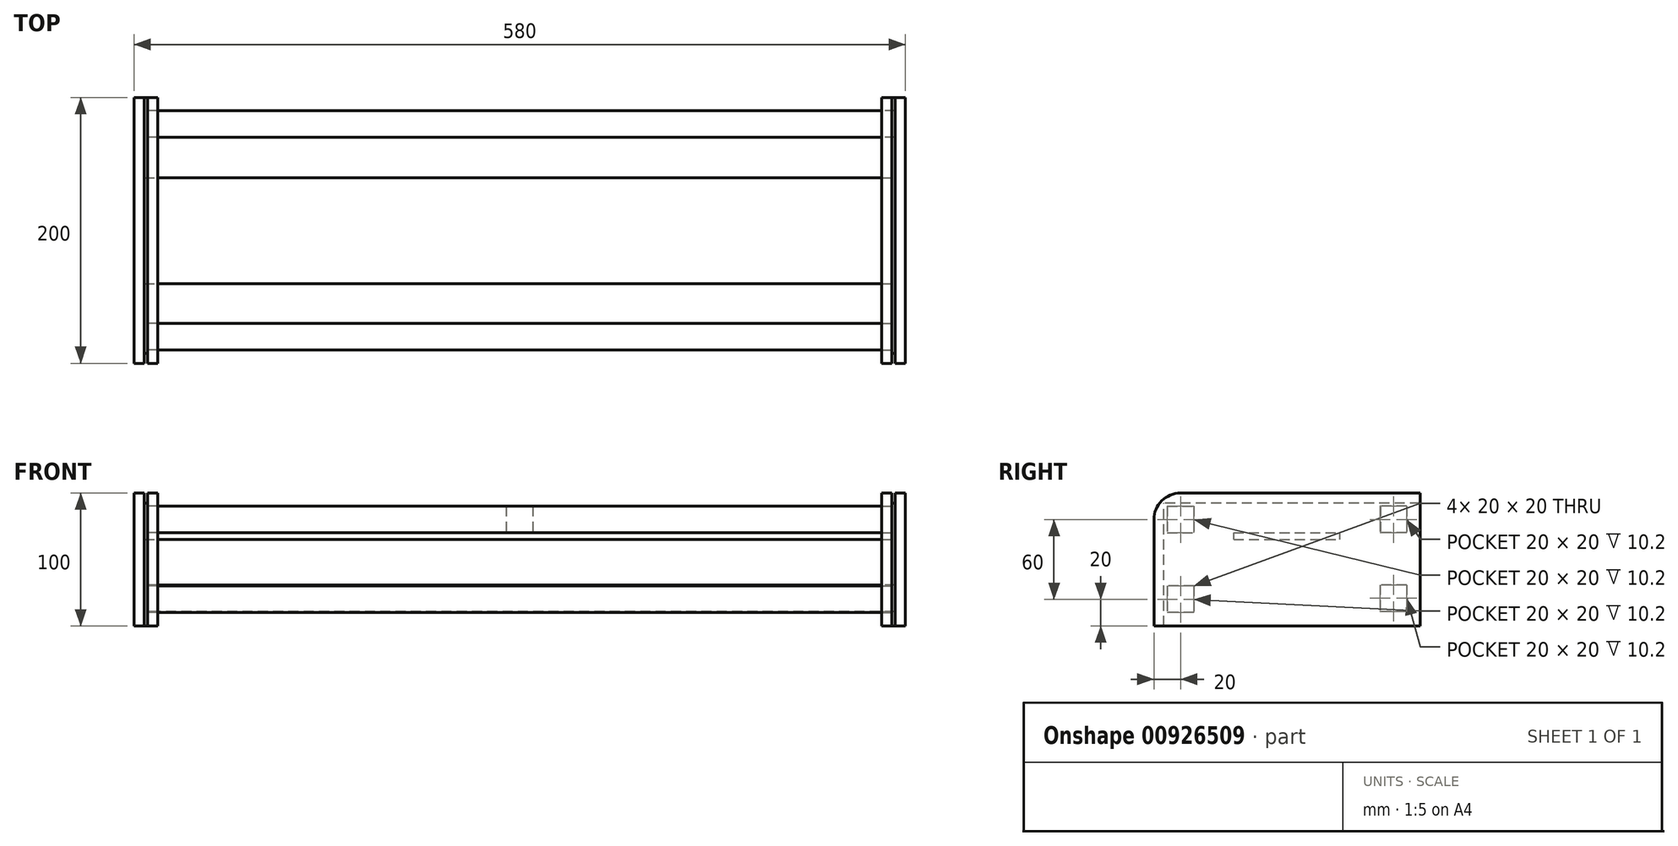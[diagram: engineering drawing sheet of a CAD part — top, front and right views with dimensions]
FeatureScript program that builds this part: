
annotation { "Feature Type Name" : "Feature", "Feature Type Description" : "" }
export const myFeature = defineFeature(function(context is Context, id is Id, definition is map)
    precondition{}
    {
        {
            var Q0;
            Q0=qCreatedBy(makeId("Right.planeOp"),FACE);
            var sketch = newSketch(context, id + "F0", { "sketchPlane" : qUnion([Q0])});
            skLineSegment(sketch, "E0.bottom", {"start": v(100, -50) * mm, "end": v(-100, -50) * mm});
            skLineSegment(sketch, "E0.top", {"start": v(100, 50) * mm, "end": v(-100, 50) * mm});
            skLineSegment(sketch, "E0.left", {"start": v(100, -50) * mm, "end": v(100, 50) * mm});
            skLineSegment(sketch, "E0.right", {"start": v(-100, -50) * mm, "end": v(-100, 50) * mm});
            skPoint(sketch, "E0.middle", {"position": v(0, 0) * mm});
            skLineSegment(sketch, "E1.bottom", {"start": v(80, -30) * mm, "end": v(-80, -30) * mm});
            skLineSegment(sketch, "E1.top", {"start": v(80, 30) * mm, "end": v(-80, 30) * mm});
            skLineSegment(sketch, "E1.left", {"start": v(80, -30) * mm, "end": v(80, 30) * mm});
            skLineSegment(sketch, "E1.right", {"start": v(-80, -30) * mm, "end": v(-80, 30) * mm});
            skLineSegment(sketch, "E2.right", {"start": v(-90, -36.84) * mm, "end": v(-80, -33.46) * mm});
            skPoint(sketch, "E2.middle", {"position": v(0, -31.3) * mm});
            skLineSegment(sketch, "E3.right", {"start": v(-89.73, 15.73) * mm, "end": v(-80, 14.19) * mm});
            skPoint(sketch, "E3.middle", {"position": v(0, 23.38) * mm});
            skLineSegment(sketch, "E4.bottom", {"start": v(16.66, -50) * mm, "end": v(-14.9, -50) * mm});
            skLineSegment(sketch, "E4.top", {"start": v(14.9, 50) * mm, "end": v(-16.66, 50) * mm});
            skLineSegment(sketch, "E5.left", {"start": v(100, -5.01) * mm, "end": v(100, 5.01) * mm});
            skLineSegment(sketch, "E5.right", {"start": v(-100, -5.01) * mm, "end": v(-100, 5.01) * mm});
            skLineSegment(sketch, "E6.bottom", {"start": v(70, 20) * mm, "end": v(90, 20) * mm});
            skLineSegment(sketch, "E6.top", {"start": v(70, 40) * mm, "end": v(90, 40) * mm});
            skLineSegment(sketch, "E6.left", {"start": v(70, 20) * mm, "end": v(70, 40) * mm});
            skLineSegment(sketch, "E6.right", {"start": v(90, 20) * mm, "end": v(90, 40) * mm});
            skPoint(sketch, "E6.middle", {"position": v(80, 30) * mm});
            skLineSegment(sketch, "E7.bottom", {"start": v(-70, 20) * mm, "end": v(-90, 20) * mm});
            skLineSegment(sketch, "E7.top", {"start": v(-70, 40) * mm, "end": v(-90, 40) * mm});
            skLineSegment(sketch, "E7.left", {"start": v(-70, 20) * mm, "end": v(-70, 40) * mm});
            skLineSegment(sketch, "E7.right", {"start": v(-90, 20) * mm, "end": v(-90, 40) * mm});
            skPoint(sketch, "E7.middle", {"position": v(-80, 30) * mm});
            skLineSegment(sketch, "E8.bottom", {"start": v(-90, -40) * mm, "end": v(-70, -40) * mm});
            skLineSegment(sketch, "E8.top", {"start": v(-90, -20) * mm, "end": v(-70, -20) * mm});
            skLineSegment(sketch, "E8.left", {"start": v(-90, -40) * mm, "end": v(-90, -20) * mm});
            skLineSegment(sketch, "E8.right", {"start": v(-70, -40) * mm, "end": v(-70, -20) * mm});
            skPoint(sketch, "E8.middle", {"position": v(-80, -30) * mm});
            skLineSegment(sketch, "E9.bottom", {"start": v(70, -39.16) * mm, "end": v(90, -39.16) * mm});
            skLineSegment(sketch, "E9.top", {"start": v(70, -19.16) * mm, "end": v(90, -19.16) * mm});
            skLineSegment(sketch, "E9.left", {"start": v(70, -39.16) * mm, "end": v(70, -19.16) * mm});
            skLineSegment(sketch, "E9.right", {"start": v(90, -39.16) * mm, "end": v(90, -19.16) * mm});
            skPoint(sketch, "E9.middle", {"position": v(80, -29.16) * mm});
            skSolve(sketch);
        }
        {
            var Q0;
            {var subQ10=sQuery(id+"F0.wireOp",EDGE,"E0.left");Q0=makeQuery(id+"F0.imprint","IMPRINT",FACE,{"disambiguationData":[TD([[makeQuery(id+"F0.imprint","IMPRINT",EDGE,{"derivedFrom":subQ10}),1.0]])]});}
            var Q1;
            {var subQ14=sQuery(id+"F0.wireOp",EDGE,"E0.right");Q1=makeQuery(id+"F0.imprint","IMPRINT",FACE,{"disambiguationData":[TD([[makeQuery(id+"F0.imprint","IMPRINT",EDGE,{"derivedFrom":subQ14}),-1.0]])]});}
            var Q2;
            {var subQ1=sQuery(id+"F0.wireOp",EDGE,"E4.top");Q2=makeQuery(id+"F0.imprint","IMPRINT",FACE,{"disambiguationData":[TD([[makeQuery(id+"F0.imprint","IMPRINT",EDGE,{"derivedFrom":subQ1}),1.0]])]});}
            var Q3;
            {var subQ0=sQuery(id+"F0.wireOp",EDGE,"E3.top");var subQ1=sQuery(id+"F0.wireOp",EDGE,"ilXIjhRa-h4DM-NYfa-dKmE-4tYrYaVo3qCb");var subQ2=makeQuery(id+"F0.imprint","INTERSECT",VERTEX,{"disambiguationData":[OD(1.0)],"derivedFrom":[subQ1,subQ0]});Q3=makeQuery(id+"F0.imprint","IMPRINT",FACE,{"disambiguationData":[TD([[makeQuery(id+"F0.imprint","IMPRINT",EDGE,{"disambiguationData":[TD([[subQ2,-1.0]])],"derivedFrom":subQ1}),1.0]])]});}
            var Q4;
            {var subQ0=sQuery(id+"F0.wireOp",EDGE,"E3.bottom");var subQ1=sQuery(id+"F0.wireOp",EDGE,"ilXIjhRa-h4DM-NYfa-dKmE-4tYrYaVo3qCb");var subQ2=makeQuery(id+"F0.imprint","INTERSECT",VERTEX,{"disambiguationData":[OD(1.0)],"derivedFrom":[subQ1,subQ0]});Q4=makeQuery(id+"F0.imprint","IMPRINT",FACE,{"disambiguationData":[TD([[makeQuery(id+"F0.imprint","IMPRINT",EDGE,{"disambiguationData":[TD([[subQ2,-1.0]])],"derivedFrom":subQ1}),1.0]])]});}
            var Q5;
            {var subQ0=sQuery(id+"F0.wireOp",EDGE,"E2.top");var subQ1=sQuery(id+"F0.wireOp",EDGE,"ilXIjhRa-h4DM-NYfa-dKmE-4tYrYaVo3qCb");var subQ2=makeQuery(id+"F0.imprint","INTERSECT",VERTEX,{"disambiguationData":[OD(0.0)],"derivedFrom":[subQ1,subQ0]});Q5=makeQuery(id+"F0.imprint","IMPRINT",FACE,{"disambiguationData":[TD([[makeQuery(id+"F0.imprint","IMPRINT",EDGE,{"disambiguationData":[TD([[subQ2,-1.0]])],"derivedFrom":subQ1}),1.0]])]});}
            var Q6;
            {var subQ0=sQuery(id+"F0.wireOp",EDGE,"E4.bottom");Q6=makeQuery(id+"F0.imprint","IMPRINT",FACE,{"disambiguationData":[TD([[makeQuery(id+"F0.imprint","IMPRINT",EDGE,{"derivedFrom":subQ0}),-1.0]])]});}
            var Q7;
            {var subQ0=sQuery(id+"F0.wireOp",EDGE,"E2.bottom");var subQ1=sQuery(id+"F0.wireOp",EDGE,"ilXIjhRa-h4DM-NYfa-dKmE-4tYrYaVo3qCb");var subQ2=makeQuery(id+"F0.imprint","INTERSECT",VERTEX,{"disambiguationData":[OD(1.0)],"derivedFrom":[subQ1,subQ0]});Q7=makeQuery(id+"F0.imprint","IMPRINT",FACE,{"disambiguationData":[TD([[makeQuery(id+"F0.imprint","IMPRINT",EDGE,{"disambiguationData":[TD([[subQ2,-1.0]])],"derivedFrom":subQ1}),1.0]])]});}
            var Q8;
            {var subQ0=sQuery(id+"F0.wireOp",EDGE,"E3.top");var subQ1=sQuery(id+"F0.wireOp",EDGE,"ilXIjhRa-h4DM-NYfa-dKmE-4tYrYaVo3qCb");var subQ2=makeQuery(id+"F0.imprint","INTERSECT",VERTEX,{"disambiguationData":[OD(0.0)],"derivedFrom":[subQ1,subQ0]});Q8=makeQuery(id+"F0.imprint","IMPRINT",FACE,{"disambiguationData":[TD([[makeQuery(id+"F0.imprint","IMPRINT",EDGE,{"disambiguationData":[TD([[subQ2,1.0]])],"derivedFrom":subQ1}),1.0]])]});}
            var Q9;
            {var subQ0=sQuery(id+"F0.wireOp",EDGE,"E3.bottom");var subQ1=sQuery(id+"F0.wireOp",EDGE,"ilXIjhRa-h4DM-NYfa-dKmE-4tYrYaVo3qCb");var subQ2=makeQuery(id+"F0.imprint","INTERSECT",VERTEX,{"disambiguationData":[OD(0.0)],"derivedFrom":[subQ1,subQ0]});Q9=makeQuery(id+"F0.imprint","IMPRINT",FACE,{"disambiguationData":[TD([[makeQuery(id+"F0.imprint","IMPRINT",EDGE,{"disambiguationData":[TD([[subQ2,1.0]])],"derivedFrom":subQ1}),1.0]])]});}
            var Q10;
            {var subQ0=sQuery(id+"F0.wireOp",EDGE,"E4.left");var subQ1=sQuery(id+"F0.wireOp",EDGE,"E3.bottom");var subQ2=makeQuery(id+"F0.imprint","INTERSECT",VERTEX,{"derivedFrom":[subQ1,subQ0]});Q10=makeQuery(id+"F0.imprint","IMPRINT",FACE,{"disambiguationData":[TD([[makeQuery(id+"F0.imprint","IMPRINT",EDGE,{"disambiguationData":[TD([[subQ2,-1.0]])],"derivedFrom":subQ1}),-1.0]])]});}
            var Q11;
            {var subQ1=sQuery(id+"F0.wireOp",EDGE,"qJEwsRZI-Cwcr-TwOn-KfsY-0AIqheChsfac");var subQ7=makeQuery(id+"F0.imprint","INTERSECT",VERTEX,{"derivedFrom":[sQuery(id+"F0.wireOp",EDGE,"E1.top"),subQ1]});Q11=makeQuery(id+"F0.imprint","IMPRINT",FACE,{"disambiguationData":[TD([[makeQuery(id+"F0.imprint","IMPRINT",EDGE,{"disambiguationData":[TD([[subQ7,1.0]])],"derivedFrom":subQ1}),1.0]])]});}
            var Q12;
            {var subQ5=sQuery(id+"F0.wireOp",EDGE,"qJEwsRZI-Cwcr-TwOn-KfsY-0AIqheChsfac");var subQ7=makeQuery(id+"F0.imprint","INTERSECT",VERTEX,{"derivedFrom":[sQuery(id+"F0.wireOp",EDGE,"E1.bottom"),subQ5]});Q12=makeQuery(id+"F0.imprint","IMPRINT",FACE,{"disambiguationData":[TD([[makeQuery(id+"F0.imprint","IMPRINT",EDGE,{"disambiguationData":[TD([[subQ7,1.0]])],"derivedFrom":subQ5}),1.0]])]});}
            var Q13;
            {var subQ0=sQuery(id+"F0.wireOp",EDGE,"E4.left");var subQ1=sQuery(id+"F0.wireOp",EDGE,"E2.top");var subQ2=makeQuery(id+"F0.imprint","INTERSECT",VERTEX,{"derivedFrom":[subQ1,subQ0]});Q13=makeQuery(id+"F0.imprint","IMPRINT",FACE,{"disambiguationData":[TD([[makeQuery(id+"F0.imprint","IMPRINT",EDGE,{"disambiguationData":[TD([[subQ2,-1.0]])],"derivedFrom":subQ1}),-1.0]])]});}
            var Q14;
            {var subQ0=sQuery(id+"F0.wireOp",EDGE,"E2.top");var subQ1=sQuery(id+"F0.wireOp",EDGE,"qJEwsRZI-Cwcr-TwOn-KfsY-0AIqheChsfac");var subQ2=makeQuery(id+"F0.imprint","INTERSECT",VERTEX,{"disambiguationData":[OD(0.0)],"derivedFrom":[subQ1,subQ0]});Q14=makeQuery(id+"F0.imprint","IMPRINT",FACE,{"disambiguationData":[TD([[makeQuery(id+"F0.imprint","IMPRINT",EDGE,{"disambiguationData":[TD([[subQ2,-1.0]])],"derivedFrom":subQ1}),1.0]])]});}
            var Q15;
            {var subQ0=sQuery(id+"F0.wireOp",EDGE,"E2.bottom");var subQ1=sQuery(id+"F0.wireOp",EDGE,"qJEwsRZI-Cwcr-TwOn-KfsY-0AIqheChsfac");var subQ2=makeQuery(id+"F0.imprint","INTERSECT",VERTEX,{"disambiguationData":[OD(1.0)],"derivedFrom":[subQ1,subQ0]});Q15=makeQuery(id+"F0.imprint","IMPRINT",FACE,{"disambiguationData":[TD([[makeQuery(id+"F0.imprint","IMPRINT",EDGE,{"disambiguationData":[TD([[subQ2,-1.0]])],"derivedFrom":subQ1}),1.0]])]});}
            var Q16;
            {var subQ3=sQuery(id+"F0.wireOp",EDGE,"E3.bottom");var subQ5=sQuery(id+"F0.wireOp",EDGE,"ilXIjhRa-h4DM-NYfa-dKmE-4tYrYaVo3qCb");var subQ7=makeQuery(id+"F0.imprint","INTERSECT",VERTEX,{"disambiguationData":[OD(1.0)],"derivedFrom":[subQ5,subQ3]});Q16=makeQuery(id+"F0.imprint","IMPRINT",FACE,{"disambiguationData":[TD([[makeQuery(id+"F0.imprint","IMPRINT",EDGE,{"disambiguationData":[TD([[subQ7,-1.0]])],"derivedFrom":subQ5}),-1.0]])]});}
            var Q17;
            {var subQ3=sQuery(id+"F0.wireOp",EDGE,"E3.bottom");var subQ5=sQuery(id+"F0.wireOp",EDGE,"ilXIjhRa-h4DM-NYfa-dKmE-4tYrYaVo3qCb");var subQ6=makeQuery(id+"F0.imprint","INTERSECT",VERTEX,{"disambiguationData":[OD(0.0)],"derivedFrom":[subQ5,subQ3]});Q17=makeQuery(id+"F0.imprint","IMPRINT",FACE,{"disambiguationData":[TD([[makeQuery(id+"F0.imprint","IMPRINT",EDGE,{"disambiguationData":[TD([[subQ6,1.0]])],"derivedFrom":subQ5}),-1.0]])]});}
            var Q18;
            {var subQ0=sQuery(id+"F0.wireOp",EDGE,"E3.bottom");var subQ1=sQuery(id+"F0.wireOp",EDGE,"qJEwsRZI-Cwcr-TwOn-KfsY-0AIqheChsfac");var subQ2=makeQuery(id+"F0.imprint","INTERSECT",VERTEX,{"disambiguationData":[OD(1.0)],"derivedFrom":[subQ1,subQ0]});Q18=makeQuery(id+"F0.imprint","IMPRINT",FACE,{"disambiguationData":[TD([[makeQuery(id+"F0.imprint","IMPRINT",EDGE,{"disambiguationData":[TD([[subQ2,-1.0]])],"derivedFrom":subQ1}),1.0]])]});}
            var Q19;
            {var subQ0=sQuery(id+"F0.wireOp",EDGE,"E3.bottom");var subQ1=sQuery(id+"F0.wireOp",EDGE,"qJEwsRZI-Cwcr-TwOn-KfsY-0AIqheChsfac");var subQ2=makeQuery(id+"F0.imprint","INTERSECT",VERTEX,{"disambiguationData":[OD(0.0)],"derivedFrom":[subQ1,subQ0]});Q19=makeQuery(id+"F0.imprint","IMPRINT",FACE,{"disambiguationData":[TD([[makeQuery(id+"F0.imprint","IMPRINT",EDGE,{"disambiguationData":[TD([[subQ2,1.0]])],"derivedFrom":subQ1}),1.0]])]});}
            var Q20;
            {var subQ0=sQuery(id+"F0.wireOp",EDGE,"E3.top");var subQ1=sQuery(id+"F0.wireOp",EDGE,"qJEwsRZI-Cwcr-TwOn-KfsY-0AIqheChsfac");var subQ2=makeQuery(id+"F0.imprint","INTERSECT",VERTEX,{"disambiguationData":[OD(0.0)],"derivedFrom":[subQ1,subQ0]});Q20=makeQuery(id+"F0.imprint","IMPRINT",FACE,{"disambiguationData":[TD([[makeQuery(id+"F0.imprint","IMPRINT",EDGE,{"disambiguationData":[TD([[subQ2,-1.0]])],"derivedFrom":subQ1}),1.0]])]});}
            var Q21;
            {var subQ0=sQuery(id+"F0.wireOp",EDGE,"E4.right");var subQ1=sQuery(id+"F0.wireOp",EDGE,"qJEwsRZI-Cwcr-TwOn-KfsY-0AIqheChsfac");var subQ2=makeQuery(id+"F0.imprint","INTERSECT",VERTEX,{"disambiguationData":[OD(0.0)],"derivedFrom":[subQ1,subQ0]});Q21=makeQuery(id+"F0.imprint","IMPRINT",FACE,{"disambiguationData":[TD([[makeQuery(id+"F0.imprint","IMPRINT",EDGE,{"disambiguationData":[TD([[subQ2,-1.0]])],"derivedFrom":subQ1}),1.0]])]});}
            var Q22;
            {var subQ0=sQuery(id+"F0.wireOp",EDGE,"E4.left");var subQ1=sQuery(id+"F0.wireOp",EDGE,"qJEwsRZI-Cwcr-TwOn-KfsY-0AIqheChsfac");var subQ2=makeQuery(id+"F0.imprint","INTERSECT",VERTEX,{"disambiguationData":[OD(1.0)],"derivedFrom":[subQ1,subQ0]});Q22=makeQuery(id+"F0.imprint","IMPRINT",FACE,{"disambiguationData":[TD([[makeQuery(id+"F0.imprint","IMPRINT",EDGE,{"disambiguationData":[TD([[subQ2,-1.0]])],"derivedFrom":subQ1}),1.0]])]});}
            var Q23;
            {var subQ0=sQuery(id+"F0.wireOp",EDGE,"E2.bottom");var subQ1=sQuery(id+"F0.wireOp",EDGE,"qJEwsRZI-Cwcr-TwOn-KfsY-0AIqheChsfac");var subQ2=makeQuery(id+"F0.imprint","INTERSECT",VERTEX,{"disambiguationData":[OD(0.0)],"derivedFrom":[subQ1,subQ0]});Q23=makeQuery(id+"F0.imprint","IMPRINT",FACE,{"disambiguationData":[TD([[makeQuery(id+"F0.imprint","IMPRINT",EDGE,{"disambiguationData":[TD([[subQ2,-1.0]])],"derivedFrom":subQ1}),1.0]])]});}
            var Q24;
            {var subQ0=sQuery(id+"F0.wireOp",EDGE,"c1IAvuGv-3G2W-eEcT-URjF-tdlOrtGlBp0P");var subQ1=sQuery(id+"F0.wireOp",EDGE,"E0.top");var subQ2=makeQuery(id+"F0.imprint","INTERSECT",VERTEX,{"disambiguationData":[OD(1.0)],"derivedFrom":[subQ1,subQ0]});Q24=makeQuery(id+"F0.imprint","IMPRINT",FACE,{"disambiguationData":[TD([[makeQuery(id+"F0.imprint","IMPRINT",EDGE,{"disambiguationData":[TD([[subQ2,1.0]])],"derivedFrom":subQ1}),1.0]])]});}
            var Q25;
            {var subQ0=sQuery(id+"F0.wireOp",EDGE,"c1IAvuGv-3G2W-eEcT-URjF-tdlOrtGlBp0P");var subQ1=sQuery(id+"F0.wireOp",EDGE,"E0.top");var subQ2=makeQuery(id+"F0.imprint","INTERSECT",VERTEX,{"disambiguationData":[OD(0.0)],"derivedFrom":[subQ1,subQ0]});Q25=makeQuery(id+"F0.imprint","IMPRINT",FACE,{"disambiguationData":[TD([[makeQuery(id+"F0.imprint","IMPRINT",EDGE,{"disambiguationData":[TD([[subQ2,-1.0]])],"derivedFrom":subQ1}),1.0]])]});}
            var Q26;
            {var subQ0=sQuery(id+"F0.wireOp",EDGE,"c1IAvuGv-3G2W-eEcT-URjF-tdlOrtGlBp0P");var subQ1=sQuery(id+"F0.wireOp",EDGE,"E0.bottom");var subQ2=makeQuery(id+"F0.imprint","INTERSECT",VERTEX,{"disambiguationData":[OD(0.0)],"derivedFrom":[subQ1,subQ0]});Q26=makeQuery(id+"F0.imprint","IMPRINT",FACE,{"disambiguationData":[TD([[makeQuery(id+"F0.imprint","IMPRINT",EDGE,{"disambiguationData":[TD([[subQ2,-1.0]])],"derivedFrom":subQ1}),-1.0]])]});}
            var Q27;
            {var subQ0=sQuery(id+"F0.wireOp",EDGE,"c1IAvuGv-3G2W-eEcT-URjF-tdlOrtGlBp0P");var subQ1=sQuery(id+"F0.wireOp",EDGE,"E0.bottom");var subQ2=makeQuery(id+"F0.imprint","INTERSECT",VERTEX,{"disambiguationData":[OD(1.0)],"derivedFrom":[subQ1,subQ0]});Q27=makeQuery(id+"F0.imprint","IMPRINT",FACE,{"disambiguationData":[TD([[makeQuery(id+"F0.imprint","IMPRINT",EDGE,{"disambiguationData":[TD([[subQ2,1.0]])],"derivedFrom":subQ1}),-1.0]])]});}
            var Q28;
            {var subQ1=sQuery(id+"F0.wireOp",EDGE,"E2.bottom");var subQ3=sQuery(id+"F0.wireOp",EDGE,"c1IAvuGv-3G2W-eEcT-URjF-tdlOrtGlBp0P");var subQ4=makeQuery(id+"F0.imprint","INTERSECT",VERTEX,{"disambiguationData":[OD(1.0)],"derivedFrom":[subQ1,subQ3]});Q28=makeQuery(id+"F0.imprint","IMPRINT",FACE,{"disambiguationData":[TD([[makeQuery(id+"F0.imprint","IMPRINT",EDGE,{"disambiguationData":[TD([[subQ4,1.0]])],"derivedFrom":subQ3}),-1.0]])]});}
            var Q29;
            {var subQ1=sQuery(id+"F0.wireOp",EDGE,"E2.bottom");var subQ3=sQuery(id+"F0.wireOp",EDGE,"c1IAvuGv-3G2W-eEcT-URjF-tdlOrtGlBp0P");var subQ4=makeQuery(id+"F0.imprint","INTERSECT",VERTEX,{"disambiguationData":[OD(0.0)],"derivedFrom":[subQ1,subQ3]});Q29=makeQuery(id+"F0.imprint","IMPRINT",FACE,{"disambiguationData":[TD([[makeQuery(id+"F0.imprint","IMPRINT",EDGE,{"disambiguationData":[TD([[subQ4,-1.0]])],"derivedFrom":subQ3}),-1.0]])]});}
            var Q30;
            {var subQ7=sQuery(id+"F0.wireOp",EDGE,"E0.right");var subQ8=sQuery(id+"F0.wireOp",EDGE,"E0.bottom");var subQ9=makeQuery(id+"F0.imprint","INTERSECT",VERTEX,{"derivedFrom":[subQ8,subQ7]});Q30=makeQuery(id+"F0.imprint","IMPRINT",FACE,{"disambiguationData":[TD([[makeQuery(id+"F0.imprint","IMPRINT",EDGE,{"disambiguationData":[TD([[subQ9,1.0]])],"derivedFrom":subQ8}),-1.0]])]});}
            var Q31;
            {var subQ5=sQuery(id+"F0.wireOp",EDGE,"E5.right");Q31=makeQuery(id+"F0.imprint","IMPRINT",FACE,{"disambiguationData":[TD([[makeQuery(id+"F0.imprint","IMPRINT",EDGE,{"derivedFrom":subQ5}),-1.0]])]});}
            var Q32;
            {var subQ7=sQuery(id+"F0.wireOp",EDGE,"E0.bottom");var subQ9=sQuery(id+"F0.wireOp",EDGE,"E0.left");var subQ10=makeQuery(id+"F0.imprint","INTERSECT",VERTEX,{"derivedFrom":[subQ7,subQ9]});Q32=makeQuery(id+"F0.imprint","IMPRINT",FACE,{"disambiguationData":[TD([[makeQuery(id+"F0.imprint","IMPRINT",EDGE,{"disambiguationData":[TD([[subQ10,-1.0]])],"derivedFrom":subQ7}),-1.0]])]});}
            var Q33;
            {var subQ5=sQuery(id+"F0.wireOp",EDGE,"E5.left");Q33=makeQuery(id+"F0.imprint","IMPRINT",FACE,{"disambiguationData":[TD([[makeQuery(id+"F0.imprint","IMPRINT",EDGE,{"derivedFrom":subQ5}),1.0]])]});}
            var Q34;
            {var subQ0=sQuery(id+"F0.wireOp",EDGE,"E5.top");var subQ1=sQuery(id+"F0.wireOp",EDGE,"ilXIjhRa-h4DM-NYfa-dKmE-4tYrYaVo3qCb");var subQ2=makeQuery(id+"F0.imprint","INTERSECT",VERTEX,{"disambiguationData":[OD(0.0)],"derivedFrom":[subQ1,subQ0]});Q34=makeQuery(id+"F0.imprint","IMPRINT",FACE,{"disambiguationData":[TD([[makeQuery(id+"F0.imprint","IMPRINT",EDGE,{"disambiguationData":[TD([[subQ2,1.0]])],"derivedFrom":subQ1}),1.0]])]});}
            var Q35;
            {var subQ0=sQuery(id+"F0.wireOp",EDGE,"E2.top");var subQ1=sQuery(id+"F0.wireOp",EDGE,"ilXIjhRa-h4DM-NYfa-dKmE-4tYrYaVo3qCb");var subQ2=makeQuery(id+"F0.imprint","INTERSECT",VERTEX,{"disambiguationData":[OD(1.0)],"derivedFrom":[subQ1,subQ0]});Q35=makeQuery(id+"F0.imprint","IMPRINT",FACE,{"disambiguationData":[TD([[makeQuery(id+"F0.imprint","IMPRINT",EDGE,{"disambiguationData":[TD([[subQ2,-1.0]])],"derivedFrom":subQ1}),1.0]])]});}
            var Q36;
            {var subQ0=sQuery(id+"F0.wireOp",EDGE,"E5.bottom");var subQ1=sQuery(id+"F0.wireOp",EDGE,"ilXIjhRa-h4DM-NYfa-dKmE-4tYrYaVo3qCb");var subQ2=makeQuery(id+"F0.imprint","INTERSECT",VERTEX,{"disambiguationData":[OD(0.0)],"derivedFrom":[subQ1,subQ0]});Q36=makeQuery(id+"F0.imprint","IMPRINT",FACE,{"disambiguationData":[TD([[makeQuery(id+"F0.imprint","IMPRINT",EDGE,{"disambiguationData":[TD([[subQ2,-1.0]])],"derivedFrom":subQ1}),1.0]])]});}
            var Q37;
            {var subQ0=sQuery(id+"F0.wireOp",EDGE,"E5.top");var subQ1=sQuery(id+"F0.wireOp",EDGE,"ilXIjhRa-h4DM-NYfa-dKmE-4tYrYaVo3qCb");var subQ2=makeQuery(id+"F0.imprint","INTERSECT",VERTEX,{"disambiguationData":[OD(1.0)],"derivedFrom":[subQ1,subQ0]});Q37=makeQuery(id+"F0.imprint","IMPRINT",FACE,{"disambiguationData":[TD([[makeQuery(id+"F0.imprint","IMPRINT",EDGE,{"disambiguationData":[TD([[subQ2,-1.0]])],"derivedFrom":subQ1}),1.0]])]});}
            var Q38;
            {var subQ0=sQuery(id+"F0.wireOp",EDGE,"E4.left");var subQ1=sQuery(id+"F0.wireOp",EDGE,"E3.bottom");var subQ2=makeQuery(id+"F0.imprint","INTERSECT",VERTEX,{"derivedFrom":[subQ1,subQ0]});Q38=makeQuery(id+"F0.imprint","IMPRINT",FACE,{"disambiguationData":[TD([[makeQuery(id+"F0.imprint","IMPRINT",EDGE,{"disambiguationData":[TD([[subQ2,-1.0]])],"derivedFrom":subQ1}),1.0]])]});}
            var Q39;
            {var subQ0=sQuery(id+"F0.wireOp",EDGE,"E2.top");var subQ1=sQuery(id+"F0.wireOp",EDGE,"qJEwsRZI-Cwcr-TwOn-KfsY-0AIqheChsfac");var subQ2=makeQuery(id+"F0.imprint","INTERSECT",VERTEX,{"disambiguationData":[OD(1.0)],"derivedFrom":[subQ1,subQ0]});Q39=makeQuery(id+"F0.imprint","IMPRINT",FACE,{"disambiguationData":[TD([[makeQuery(id+"F0.imprint","IMPRINT",EDGE,{"disambiguationData":[TD([[subQ2,-1.0]])],"derivedFrom":subQ1}),1.0]])]});}
            var Q40;
            {var subQ0=sQuery(id+"F0.wireOp",EDGE,"E5.bottom");var subQ1=sQuery(id+"F0.wireOp",EDGE,"qJEwsRZI-Cwcr-TwOn-KfsY-0AIqheChsfac");var subQ2=makeQuery(id+"F0.imprint","INTERSECT",VERTEX,{"disambiguationData":[OD(0.0)],"derivedFrom":[subQ1,subQ0]});Q40=makeQuery(id+"F0.imprint","IMPRINT",FACE,{"disambiguationData":[TD([[makeQuery(id+"F0.imprint","IMPRINT",EDGE,{"disambiguationData":[TD([[subQ2,-1.0]])],"derivedFrom":subQ1}),1.0]])]});}
            var Q41;
            {var subQ3=sQuery(id+"F0.wireOp",EDGE,"E5.bottom");var subQ5=sQuery(id+"F0.wireOp",EDGE,"ilXIjhRa-h4DM-NYfa-dKmE-4tYrYaVo3qCb");var subQ6=makeQuery(id+"F0.imprint","INTERSECT",VERTEX,{"disambiguationData":[OD(0.0)],"derivedFrom":[subQ5,subQ3]});Q41=makeQuery(id+"F0.imprint","IMPRINT",FACE,{"disambiguationData":[TD([[makeQuery(id+"F0.imprint","IMPRINT",EDGE,{"disambiguationData":[TD([[subQ6,-1.0]])],"derivedFrom":subQ5}),-1.0]])]});}
            var Q42;
            {var subQ0=sQuery(id+"F0.wireOp",EDGE,"E2.top");var subQ5=sQuery(id+"F0.wireOp",EDGE,"ilXIjhRa-h4DM-NYfa-dKmE-4tYrYaVo3qCb");var subQ6=makeQuery(id+"F0.imprint","INTERSECT",VERTEX,{"disambiguationData":[OD(1.0)],"derivedFrom":[subQ5,subQ0]});Q42=makeQuery(id+"F0.imprint","IMPRINT",FACE,{"disambiguationData":[TD([[makeQuery(id+"F0.imprint","IMPRINT",EDGE,{"disambiguationData":[TD([[subQ6,-1.0]])],"derivedFrom":subQ5}),-1.0]])]});}
            var Q43;
            {var subQ0=sQuery(id+"F0.wireOp",EDGE,"E2.right");var subQ5=sQuery(id+"F0.wireOp",EDGE,"c1IAvuGv-3G2W-eEcT-URjF-tdlOrtGlBp0P");var subQ6=makeQuery(id+"F0.imprint","INTERSECT",VERTEX,{"derivedFrom":[subQ0,subQ5]});Q43=makeQuery(id+"F0.imprint","IMPRINT",FACE,{"disambiguationData":[TD([[makeQuery(id+"F0.imprint","IMPRINT",EDGE,{"disambiguationData":[TD([[subQ6,1.0]])],"derivedFrom":subQ5}),1.0]])]});}
            var Q44;
            {var subQ0=sQuery(id+"F0.wireOp",EDGE,"E2.left");var subQ5=sQuery(id+"F0.wireOp",EDGE,"c1IAvuGv-3G2W-eEcT-URjF-tdlOrtGlBp0P");var subQ6=makeQuery(id+"F0.imprint","INTERSECT",VERTEX,{"derivedFrom":[subQ0,subQ5]});Q44=makeQuery(id+"F0.imprint","IMPRINT",FACE,{"disambiguationData":[TD([[makeQuery(id+"F0.imprint","IMPRINT",EDGE,{"disambiguationData":[TD([[subQ6,-1.0]])],"derivedFrom":subQ5}),1.0]])]});}
            var Q45;
            {var subQ0=sQuery(id+"F0.wireOp",EDGE,"E3.left");Q45=makeQuery(id+"F0.imprint","IMPRINT",FACE,{"disambiguationData":[TD([[makeQuery(id+"F0.imprint","IMPRINT",EDGE,{"derivedFrom":subQ0}),-1.0]])]});}
            var Q46;
            {var subQ0=sQuery(id+"F0.wireOp",EDGE,"E3.right");Q46=makeQuery(id+"F0.imprint","IMPRINT",FACE,{"disambiguationData":[TD([[makeQuery(id+"F0.imprint","IMPRINT",EDGE,{"derivedFrom":subQ0}),1.0]])]});}
            var Q47;
            {var subQ5=sQuery(id+"F0.wireOp",EDGE,"E1.right");var subQ7=makeQuery(id+"F0.imprint","IMPRINT",VERTEX,{"derivedFrom":subQ5});Q47=makeQuery(id+"F0.imprint","IMPRINT",FACE,{"disambiguationData":[TD([[makeQuery(id+"F0.imprint","IMPRINT",EDGE,{"disambiguationData":[TD([[subQ7,1.0]])],"derivedFrom":subQ5}),-1.0]])]});}
            extrude(context, id + "F1", {"entities" : qUnion([Q0, Q1, Q2, Q3, Q4, Q5, Q6, Q7, Q8, Q9, Q10, Q11, Q12, Q13, Q14, Q15, Q16, Q17, Q18, Q19, Q20, Q21, Q22, Q23, Q24, Q25, Q26, Q27, Q28, Q29, Q30, Q31, Q32, Q33, Q34, Q35, Q36, Q37, Q38, Q39, Q40, Q41, Q42, Q43, Q44, Q45, Q46, Q47]), "oppositeDirection" : true, "depth" : 18 * mm, "offsetDistance" : 25 * mm});
        }
        {
            var Q0;
            Q0=makeQuery(id+"F1.opExtrude","SWEPT_FACE",FACE,{"disambiguationData":[OSD([sQuery(id+"F0.wireOp",EDGE,"E0.right"),sQuery(id+"F0.wireOp",EDGE,"E5.right")])]});
            var sketch = newSketch(context, id + "F2", { "sketchPlane" : qUnion([Q0])});
            skLineSegment(sketch, "E10", {"start": v(-9, 50) * mm, "end": v(-9, -50) * mm, "construction": true});
            skLineSegment(sketch, "E11", {"start": v(0, 0) * mm, "end": v(-18, 0) * mm, "construction": true});
            skLineSegment(sketch, "E12.bottom", {"start": v(-10.2, -50) * mm, "end": v(-7.8, -50) * mm, "construction": true});
            skLineSegment(sketch, "E12.top", {"start": v(-10.2, 50) * mm, "end": v(-7.8, 50) * mm, "construction": true});
            skLineSegment(sketch, "E12.left", {"start": v(-10.2, -50) * mm, "end": v(-10.2, 50) * mm});
            skLineSegment(sketch, "E12.right", {"start": v(-7.8, -50) * mm, "end": v(-7.8, 50) * mm});
            skPoint(sketch, "E12.middle", {"position": v(-9, 0) * mm});
            skLineSegment(sketch, "E13", {"start": v(0, 42.5) * mm, "end": v(-18, 42.5) * mm});
            skSolve(sketch);
        }
        {
            var Q0;
            {var subQ0=sQuery(id+"F2.wireOp",EDGE,"E12.left");var subQ3=sQuery(id+"F2.wireOp",EDGE,"E13");var subQ4=makeQuery(id+"F2.imprint","INTERSECT",VERTEX,{"derivedFrom":[subQ0,subQ3]});Q0=makeQuery(id+"F2.imprint","IMPRINT",FACE,{"disambiguationData":[TD([[makeQuery(id+"F2.imprint","IMPRINT",EDGE,{"disambiguationData":[TD([[subQ4,1.0]])],"derivedFrom":subQ3}),1.0]])]});}
            extrude(context, id + "F3", {"entities" : qUnion([Q0]), "operationType" : NewBodyOperationType.REMOVE, "oppositeDirection" : true, "depth" : 7.5 * mm, "offsetDistance" : 25 * mm});
        }
        {
            var Q0;
            {var subQ0=sQuery(id+"F2.wireOp",EDGE,"E12.left");var subQ3=sQuery(id+"F2.wireOp",EDGE,"E13");var subQ4=makeQuery(id+"F2.imprint","INTERSECT",VERTEX,{"derivedFrom":[subQ0,subQ3]});Q0=makeQuery(id+"F2.imprint","IMPRINT",FACE,{"disambiguationData":[TD([[makeQuery(id+"F2.imprint","IMPRINT",EDGE,{"disambiguationData":[TD([[subQ4,1.0]])],"derivedFrom":subQ3}),-1.0]])]});}
            var Q1;
            Q1=makeQuery(id+"F1.opExtrude","SWEPT_FACE",FACE,{"disambiguationData":[OSD([sQuery(id+"F0.wireOp",EDGE,"E0.left"),sQuery(id+"F0.wireOp",EDGE,"E5.left")])]});
            extrude(context, id + "F4", {"entities" : qUnion([Q0]), "operationType" : NewBodyOperationType.REMOVE, "endBound" : BoundingType.UP_TO_SURFACE, "oppositeDirection" : true, "depth" : 385.4 * mm, "endBoundEntityFace" : qUnion([Q1]), "offsetDistance" : 25 * mm});
        }
        {
            var Q0;
            Q0=makeQuery(id+"F1.opExtrude","SWEPT_EDGE",EDGE,{"disambiguationData":[OSD([sQuery(id+"F0.wireOp",EDGE,"E0.top"),sQuery(id+"F0.wireOp",EDGE,"E0.right")])]});
            fillet(context, id + "F5", {"entities" : qUnion([Q0]), "radius" : 20 * mm, "tangentPropagation" : true, "allowEdgeOverflow" : false});
        }
        {
            var Q0;
            {var subQ0=sQuery(id+"F0.wireOp",EDGE,"E6.top");Q0=makeQuery(id+"F0.imprint","IMPRINT",FACE,{"disambiguationData":[TD([[makeQuery(id+"F0.imprint","IMPRINT",EDGE,{"derivedFrom":subQ0}),-1.0]])]});}
            var Q1;
            {var subQ0=sQuery(id+"F0.wireOp",EDGE,"E1.left");var subQ1=sQuery(id+"F0.wireOp",EDGE,"E1.top");var subQ2=makeQuery(id+"F0.imprint","INTERSECT",VERTEX,{"derivedFrom":[subQ1,subQ0]});Q1=makeQuery(id+"F0.imprint","IMPRINT",FACE,{"disambiguationData":[TD([[makeQuery(id+"F0.imprint","IMPRINT",EDGE,{"disambiguationData":[TD([[subQ2,-1.0]])],"derivedFrom":subQ1}),1.0]])]});}
            var Q2;
            {var subQ6=sQuery(id+"F0.wireOp",EDGE,"E7.top");Q2=makeQuery(id+"F0.imprint","IMPRINT",FACE,{"disambiguationData":[TD([[makeQuery(id+"F0.imprint","IMPRINT",EDGE,{"derivedFrom":subQ6}),1.0]])]});}
            var Q3;
            {var subQ0=sQuery(id+"F0.wireOp",EDGE,"E1.right");var subQ1=sQuery(id+"F0.wireOp",EDGE,"E1.top");var subQ2=makeQuery(id+"F0.imprint","INTERSECT",VERTEX,{"derivedFrom":[subQ1,subQ0]});Q3=makeQuery(id+"F0.imprint","IMPRINT",FACE,{"disambiguationData":[TD([[makeQuery(id+"F0.imprint","IMPRINT",EDGE,{"disambiguationData":[TD([[subQ2,1.0]])],"derivedFrom":subQ1}),1.0]])]});}
            var Q4;
            {var subQ0=sQuery(id+"F0.wireOp",EDGE,"E1.right");var subQ1=sQuery(id+"F0.wireOp",EDGE,"E1.bottom");var subQ2=makeQuery(id+"F0.imprint","INTERSECT",VERTEX,{"derivedFrom":[subQ1,subQ0]});Q4=makeQuery(id+"F0.imprint","IMPRINT",FACE,{"disambiguationData":[TD([[makeQuery(id+"F0.imprint","IMPRINT",EDGE,{"disambiguationData":[TD([[subQ2,1.0]])],"derivedFrom":subQ1}),-1.0]])]});}
            var Q5;
            {var subQ5=sQuery(id+"F0.wireOp",EDGE,"E8.bottom");Q5=makeQuery(id+"F0.imprint","IMPRINT",FACE,{"disambiguationData":[TD([[makeQuery(id+"F0.imprint","IMPRINT",EDGE,{"derivedFrom":subQ5}),1.0]])]});}
            var Q6;
            {var subQ4=sQuery(id+"F0.wireOp",EDGE,"E9.bottom");Q6=makeQuery(id+"F0.imprint","IMPRINT",FACE,{"disambiguationData":[TD([[makeQuery(id+"F0.imprint","IMPRINT",EDGE,{"derivedFrom":subQ4}),1.0]])]});}
            var Q7;
            {var subQ0=sQuery(id+"F0.wireOp",EDGE,"E1.left");var subQ1=sQuery(id+"F0.wireOp",EDGE,"E1.bottom");var subQ2=makeQuery(id+"F0.imprint","INTERSECT",VERTEX,{"derivedFrom":[subQ1,subQ0]});Q7=makeQuery(id+"F0.imprint","IMPRINT",FACE,{"disambiguationData":[TD([[makeQuery(id+"F0.imprint","IMPRINT",EDGE,{"disambiguationData":[TD([[subQ2,-1.0]])],"derivedFrom":subQ1}),-1.0]])]});}
            var Q8;
            {var subQ0=sQuery(id+"F2.wireOp",EDGE,"E12.right");Q8=makeQuery(id+"F4.boolean.opBoolean","MERGE",FACE,{"derivedFrom":[makeQuery(id+"F3.boolean.opBoolean","COPY",FACE,{"derivedFrom":makeQuery(id+"F3.opExtrude","SWEPT_FACE",FACE,{"disambiguationData":[OSD([subQ0])]})})],"fromTools":[makeQuery(id+"F4.opExtrude","SWEPT_FACE",FACE,{"disambiguationData":[OSD([subQ0])]})]});}
            extrude(context, id + "F6", {"entities" : qUnion([Q0, Q1, Q2, Q3, Q4, Q5, Q6, Q7]), "operationType" : NewBodyOperationType.ADD, "endBound" : BoundingType.UP_TO_SURFACE, "oppositeDirection" : true, "depth" : 25 * mm, "endBoundEntityFace" : qUnion([Q8]), "offsetDistance" : 25 * mm});
        }
        {
            var Q0;
            Q0=makeQuery(id+"F1.opExtrude","SWEPT_BODY",BODY,{"disambiguationData":[OSD([sQuery(id+"F0.wireOp",EDGE,"E0.bottom"),sQuery(id+"F0.wireOp",EDGE,"E0.top"),sQuery(id+"F0.wireOp",EDGE,"E0.left"),sQuery(id+"F0.wireOp",EDGE,"E0.right"),sQuery(id+"F0.wireOp",EDGE,"E4.bottom"),sQuery(id+"F0.wireOp",EDGE,"E4.top"),sQuery(id+"F0.wireOp",EDGE,"E5.left"),sQuery(id+"F0.wireOp",EDGE,"E5.right"),sQuery(id+"F0.wireOp",EDGE,"E6.bottom"),sQuery(id+"F0.wireOp",EDGE,"E6.top"),sQuery(id+"F0.wireOp",EDGE,"E6.left"),sQuery(id+"F0.wireOp",EDGE,"E6.right"),sQuery(id+"F0.wireOp",EDGE,"E7.bottom"),sQuery(id+"F0.wireOp",EDGE,"E7.top"),sQuery(id+"F0.wireOp",EDGE,"E7.left"),sQuery(id+"F0.wireOp",EDGE,"E7.right"),sQuery(id+"F0.wireOp",EDGE,"E8.bottom"),sQuery(id+"F0.wireOp",EDGE,"E8.top"),sQuery(id+"F0.wireOp",EDGE,"E8.left"),sQuery(id+"F0.wireOp",EDGE,"E8.right"),sQuery(id+"F0.wireOp",EDGE,"E9.bottom"),sQuery(id+"F0.wireOp",EDGE,"E9.top"),sQuery(id+"F0.wireOp",EDGE,"E9.left"),sQuery(id+"F0.wireOp",EDGE,"E9.right")])]});
            transform(context, id + "F7", {"entities" : qUnion([Q0]), "transformType" : TransformType.TRANSLATION_3D, "dx" : 0 * mm, "dy" : 0 * mm, "dz" : 0 * mm, "makeCopy" : true});
        }
        {
            var Q0;
            Q0=makeQuery(id+"F7.opPattern","COPY",BODY,{"derivedFrom":makeQuery(id+"F1.opExtrude","SWEPT_BODY",BODY,{"disambiguationData":[OSD([sQuery(id+"F0.wireOp",EDGE,"E0.bottom"),sQuery(id+"F0.wireOp",EDGE,"E0.top"),sQuery(id+"F0.wireOp",EDGE,"E0.left"),sQuery(id+"F0.wireOp",EDGE,"E0.right"),sQuery(id+"F0.wireOp",EDGE,"E4.bottom"),sQuery(id+"F0.wireOp",EDGE,"E4.top"),sQuery(id+"F0.wireOp",EDGE,"E5.left"),sQuery(id+"F0.wireOp",EDGE,"E5.right"),sQuery(id+"F0.wireOp",EDGE,"E6.bottom"),sQuery(id+"F0.wireOp",EDGE,"E6.top"),sQuery(id+"F0.wireOp",EDGE,"E6.left"),sQuery(id+"F0.wireOp",EDGE,"E6.right"),sQuery(id+"F0.wireOp",EDGE,"E7.bottom"),sQuery(id+"F0.wireOp",EDGE,"E7.top"),sQuery(id+"F0.wireOp",EDGE,"E7.left"),sQuery(id+"F0.wireOp",EDGE,"E7.right"),sQuery(id+"F0.wireOp",EDGE,"E8.bottom"),sQuery(id+"F0.wireOp",EDGE,"E8.top"),sQuery(id+"F0.wireOp",EDGE,"E8.left"),sQuery(id+"F0.wireOp",EDGE,"E8.right"),sQuery(id+"F0.wireOp",EDGE,"E9.bottom"),sQuery(id+"F0.wireOp",EDGE,"E9.top"),sQuery(id+"F0.wireOp",EDGE,"E9.left"),sQuery(id+"F0.wireOp",EDGE,"E9.right")])]}),"instanceName":"1"});
            deleteBodies(context, id + "F8", {"entities" : qUnion([Q0])});
        }
        {
            var Q0;
            Q0=makeQuery(id+"F1.opExtrude","SWEPT_BODY",BODY,{"disambiguationData":[OSD([sQuery(id+"F0.wireOp",EDGE,"E0.bottom"),sQuery(id+"F0.wireOp",EDGE,"E0.top"),sQuery(id+"F0.wireOp",EDGE,"E0.left"),sQuery(id+"F0.wireOp",EDGE,"E0.right"),sQuery(id+"F0.wireOp",EDGE,"E4.bottom"),sQuery(id+"F0.wireOp",EDGE,"E4.top"),sQuery(id+"F0.wireOp",EDGE,"E5.left"),sQuery(id+"F0.wireOp",EDGE,"E5.right"),sQuery(id+"F0.wireOp",EDGE,"E6.bottom"),sQuery(id+"F0.wireOp",EDGE,"E6.top"),sQuery(id+"F0.wireOp",EDGE,"E6.left"),sQuery(id+"F0.wireOp",EDGE,"E6.right"),sQuery(id+"F0.wireOp",EDGE,"E7.bottom"),sQuery(id+"F0.wireOp",EDGE,"E7.top"),sQuery(id+"F0.wireOp",EDGE,"E7.left"),sQuery(id+"F0.wireOp",EDGE,"E7.right"),sQuery(id+"F0.wireOp",EDGE,"E8.bottom"),sQuery(id+"F0.wireOp",EDGE,"E8.top"),sQuery(id+"F0.wireOp",EDGE,"E8.left"),sQuery(id+"F0.wireOp",EDGE,"E8.right"),sQuery(id+"F0.wireOp",EDGE,"E9.bottom"),sQuery(id+"F0.wireOp",EDGE,"E9.top"),sQuery(id+"F0.wireOp",EDGE,"E9.left"),sQuery(id+"F0.wireOp",EDGE,"E9.right")])]});
            transform(context, id + "F9", {"entities" : qUnion([Q0]), "transformType" : TransformType.TRANSLATION_3D, "dx" : -580 * mm, "dy" : 0 * mm, "dz" : 0 * mm, "makeCopy" : true});
        }
        {
            var Q0;
            Q0=makeQuery(id+"F9.opPattern","COPY",BODY,{"derivedFrom":makeQuery(id+"F1.opExtrude","SWEPT_BODY",BODY,{"disambiguationData":[OSD([sQuery(id+"F0.wireOp",EDGE,"E0.bottom"),sQuery(id+"F0.wireOp",EDGE,"E0.top"),sQuery(id+"F0.wireOp",EDGE,"E0.left"),sQuery(id+"F0.wireOp",EDGE,"E0.right"),sQuery(id+"F0.wireOp",EDGE,"E4.bottom"),sQuery(id+"F0.wireOp",EDGE,"E4.top"),sQuery(id+"F0.wireOp",EDGE,"E5.left"),sQuery(id+"F0.wireOp",EDGE,"E5.right"),sQuery(id+"F0.wireOp",EDGE,"E6.bottom"),sQuery(id+"F0.wireOp",EDGE,"E6.top"),sQuery(id+"F0.wireOp",EDGE,"E6.left"),sQuery(id+"F0.wireOp",EDGE,"E6.right"),sQuery(id+"F0.wireOp",EDGE,"E7.bottom"),sQuery(id+"F0.wireOp",EDGE,"E7.top"),sQuery(id+"F0.wireOp",EDGE,"E7.left"),sQuery(id+"F0.wireOp",EDGE,"E7.right"),sQuery(id+"F0.wireOp",EDGE,"E8.bottom"),sQuery(id+"F0.wireOp",EDGE,"E8.top"),sQuery(id+"F0.wireOp",EDGE,"E8.left"),sQuery(id+"F0.wireOp",EDGE,"E8.right"),sQuery(id+"F0.wireOp",EDGE,"E9.bottom"),sQuery(id+"F0.wireOp",EDGE,"E9.top"),sQuery(id+"F0.wireOp",EDGE,"E9.left"),sQuery(id+"F0.wireOp",EDGE,"E9.right")])]}),"instanceName":"1"});
            var Q1;
            {var subQ0=sQuery(id+"F0.wireOp",EDGE,"E9.right");var subQ1=sQuery(id+"F0.wireOp",EDGE,"E9.left");var subQ2=sQuery(id+"F0.wireOp",EDGE,"E9.top");var subQ3=sQuery(id+"F0.wireOp",EDGE,"E9.bottom");var subQ4=sQuery(id+"F0.wireOp",EDGE,"E8.right");var subQ5=sQuery(id+"F0.wireOp",EDGE,"E8.left");var subQ6=sQuery(id+"F0.wireOp",EDGE,"E8.top");var subQ7=sQuery(id+"F0.wireOp",EDGE,"E8.bottom");var subQ8=sQuery(id+"F0.wireOp",EDGE,"E7.right");var subQ9=sQuery(id+"F0.wireOp",EDGE,"E7.left");var subQ10=sQuery(id+"F0.wireOp",EDGE,"E7.top");var subQ11=sQuery(id+"F0.wireOp",EDGE,"E7.bottom");var subQ12=sQuery(id+"F0.wireOp",EDGE,"E6.right");var subQ13=sQuery(id+"F0.wireOp",EDGE,"E6.left");var subQ14=sQuery(id+"F0.wireOp",EDGE,"E6.top");var subQ15=sQuery(id+"F0.wireOp",EDGE,"E6.bottom");Q1=makeQuery(id+"F9.opPattern","COPY",FACE,{"derivedFrom":makeQuery(id+"F6.boolean.opBoolean","MERGE",FACE,{"derivedFrom":[makeQuery(id+"F1.opExtrude","CAP_FACE",FACE,{"disambiguationData":[OSD([sQuery(id+"F0.wireOp",EDGE,"E0.bottom"),sQuery(id+"F0.wireOp",EDGE,"E0.top"),sQuery(id+"F0.wireOp",EDGE,"E0.left"),sQuery(id+"F0.wireOp",EDGE,"E0.right"),sQuery(id+"F0.wireOp",EDGE,"E4.bottom"),sQuery(id+"F0.wireOp",EDGE,"E4.top"),sQuery(id+"F0.wireOp",EDGE,"E5.left"),sQuery(id+"F0.wireOp",EDGE,"E5.right"),subQ15,subQ14,subQ13,subQ12,subQ11,subQ10,subQ9,subQ8,subQ7,subQ6,subQ5,subQ4,subQ3,subQ2,subQ1,subQ0])],"isStart":true}),makeQuery(id+"F6.opExtrude","CAP_FACE",FACE,{"disambiguationData":[OSD([subQ15,subQ14,subQ13,subQ12])],"isStart":true}),makeQuery(id+"F6.opExtrude","CAP_FACE",FACE,{"disambiguationData":[OSD([subQ11,subQ10,subQ9,subQ8])],"isStart":true}),makeQuery(id+"F6.opExtrude","CAP_FACE",FACE,{"disambiguationData":[OSD([subQ7,subQ6,subQ5,subQ4])],"isStart":true}),makeQuery(id+"F6.opExtrude","CAP_FACE",FACE,{"disambiguationData":[OSD([subQ3,subQ2,subQ1,subQ0])],"isStart":true})]}),"instanceName":"1"});}
            mirror(context, id + "F10", {"entities" : qUnion([Q0]), "mirrorPlane" : qUnion([Q1])});
        }
        {
            var Q0;
            Q0=makeQuery(id+"F9.opPattern","COPY",BODY,{"derivedFrom":makeQuery(id+"F1.opExtrude","SWEPT_BODY",BODY,{"disambiguationData":[OSD([sQuery(id+"F0.wireOp",EDGE,"E0.bottom"),sQuery(id+"F0.wireOp",EDGE,"E0.top"),sQuery(id+"F0.wireOp",EDGE,"E0.left"),sQuery(id+"F0.wireOp",EDGE,"E0.right"),sQuery(id+"F0.wireOp",EDGE,"E4.bottom"),sQuery(id+"F0.wireOp",EDGE,"E4.top"),sQuery(id+"F0.wireOp",EDGE,"E5.left"),sQuery(id+"F0.wireOp",EDGE,"E5.right"),sQuery(id+"F0.wireOp",EDGE,"E6.bottom"),sQuery(id+"F0.wireOp",EDGE,"E6.top"),sQuery(id+"F0.wireOp",EDGE,"E6.left"),sQuery(id+"F0.wireOp",EDGE,"E6.right"),sQuery(id+"F0.wireOp",EDGE,"E7.bottom"),sQuery(id+"F0.wireOp",EDGE,"E7.top"),sQuery(id+"F0.wireOp",EDGE,"E7.left"),sQuery(id+"F0.wireOp",EDGE,"E7.right"),sQuery(id+"F0.wireOp",EDGE,"E8.bottom"),sQuery(id+"F0.wireOp",EDGE,"E8.top"),sQuery(id+"F0.wireOp",EDGE,"E8.left"),sQuery(id+"F0.wireOp",EDGE,"E8.right"),sQuery(id+"F0.wireOp",EDGE,"E9.bottom"),sQuery(id+"F0.wireOp",EDGE,"E9.top"),sQuery(id+"F0.wireOp",EDGE,"E9.left"),sQuery(id+"F0.wireOp",EDGE,"E9.right")])]}),"instanceName":"1"});
            deleteBodies(context, id + "F11", {"entities" : qUnion([Q0])});
        }
        {
            var Q0;
            Q0=makeQuery(id+"F10.opPattern","COPY",FACE,{"derivedFrom":makeQuery(id+"F9.opPattern","COPY",FACE,{"derivedFrom":makeQuery(id+"F6.opExtrude","CAP_FACE",FACE,{"disambiguationData":[OSD([sQuery(id+"F0.wireOp",EDGE,"E6.bottom"),sQuery(id+"F0.wireOp",EDGE,"E6.top"),sQuery(id+"F0.wireOp",EDGE,"E6.left"),sQuery(id+"F0.wireOp",EDGE,"E6.right")])],"isStart":false}),"instanceName":"1"}),"instanceName":"1"});
            var Q1;
            Q1=makeQuery(id+"F10.opPattern","COPY",FACE,{"derivedFrom":makeQuery(id+"F9.opPattern","COPY",FACE,{"derivedFrom":makeQuery(id+"F6.opExtrude","CAP_FACE",FACE,{"disambiguationData":[OSD([sQuery(id+"F0.wireOp",EDGE,"E7.bottom"),sQuery(id+"F0.wireOp",EDGE,"E7.top"),sQuery(id+"F0.wireOp",EDGE,"E7.left"),sQuery(id+"F0.wireOp",EDGE,"E7.right")])],"isStart":false}),"instanceName":"1"}),"instanceName":"1"});
            var Q2;
            Q2=makeQuery(id+"F10.opPattern","COPY",FACE,{"derivedFrom":makeQuery(id+"F9.opPattern","COPY",FACE,{"derivedFrom":makeQuery(id+"F6.opExtrude","CAP_FACE",FACE,{"disambiguationData":[OSD([sQuery(id+"F0.wireOp",EDGE,"E8.bottom"),sQuery(id+"F0.wireOp",EDGE,"E8.top"),sQuery(id+"F0.wireOp",EDGE,"E8.left"),sQuery(id+"F0.wireOp",EDGE,"E8.right")])],"isStart":false}),"instanceName":"1"}),"instanceName":"1"});
            var Q3;
            Q3=makeQuery(id+"F10.opPattern","COPY",FACE,{"derivedFrom":makeQuery(id+"F9.opPattern","COPY",FACE,{"derivedFrom":makeQuery(id+"F6.opExtrude","CAP_FACE",FACE,{"disambiguationData":[OSD([sQuery(id+"F0.wireOp",EDGE,"E9.bottom"),sQuery(id+"F0.wireOp",EDGE,"E9.top"),sQuery(id+"F0.wireOp",EDGE,"E9.left"),sQuery(id+"F0.wireOp",EDGE,"E9.right")])],"isStart":false}),"instanceName":"1"}),"instanceName":"1"});
            var Q4;
            Q4=makeQuery(id+"F6.opExtrude","CAP_FACE",FACE,{"disambiguationData":[OSD([sQuery(id+"F0.wireOp",EDGE,"E6.bottom"),sQuery(id+"F0.wireOp",EDGE,"E6.top"),sQuery(id+"F0.wireOp",EDGE,"E6.left"),sQuery(id+"F0.wireOp",EDGE,"E6.right")])],"isStart":false});
            extrude(context, id + "F12", {"entities" : qUnion([Q0, Q1, Q2, Q3]), "endBound" : BoundingType.UP_TO_SURFACE, "depth" : 25 * mm, "endBoundEntityFace" : qUnion([Q4]), "offsetDistance" : 25 * mm});
        }
        {
            var Q0;
            Q0=makeQuery(id+"F12.opExtrude","SWEPT_FACE",FACE,{"disambiguationData":[OSD([sQuery(id+"F0.wireOp",EDGE,"E7.right")])]});
            var sketch = newSketch(context, id + "F13", { "sketchPlane" : qUnion([Q0])});
            skLineSegment(sketch, "E14.bottom", {"start": v(-572.2, 40) * mm, "end": v(-7.8, 40) * mm});
            skLineSegment(sketch, "E14.top", {"start": v(-572.2, -39.73) * mm, "end": v(-7.8, -39.73) * mm});
            skLineSegment(sketch, "E14.left", {"start": v(-572.2, 40) * mm, "end": v(-572.2, -39.73) * mm});
            skLineSegment(sketch, "E14.right", {"start": v(-7.8, 40) * mm, "end": v(-7.8, -39.73) * mm});
            skSolve(sketch);
        }
        {
            var Q0;
            Q0 = qSketchRegion(id + "F13", true);
            extrude(context, id + "F14", {"entities" : qUnion([Q0]), "depth" : 5 * mm, "offsetDistance" : 25 * mm});
        }
        {
            var Q0;
            Q0=makeQuery(id+"F12.opExtrude","SWEPT_FACE",FACE,{"disambiguationData":[OSD([sQuery(id+"F0.wireOp",EDGE,"E6.top")])]});
            var sketch = newSketch(context, id + "F15", { "sketchPlane" : qUnion([Q0])});
            skLineSegment(sketch, "E15.bottom", {"start": v(-17.3, 90) * mm, "end": v(-561.93, 90) * mm});
            skLineSegment(sketch, "E15.top", {"start": v(-17.3, -94.84) * mm, "end": v(-561.93, -94.84) * mm});
            skLineSegment(sketch, "E15.left", {"start": v(-17.3, 90) * mm, "end": v(-17.3, -94.84) * mm});
            skLineSegment(sketch, "E15.right", {"start": v(-561.93, 90) * mm, "end": v(-561.93, -94.84) * mm});
            skLineSegment(sketch, "E16", {"start": v(-290, 70) * mm, "end": v(-290, -68.91) * mm, "construction": true});
            skLineSegment(sketch, "E17.bottom", {"start": v(-280, -70.17) * mm, "end": v(-300, -70.17) * mm});
            skLineSegment(sketch, "E17.top", {"start": v(-280, 71.26) * mm, "end": v(-300, 71.26) * mm});
            skLineSegment(sketch, "E17.left", {"start": v(-280, -70.17) * mm, "end": v(-280, 71.26) * mm});
            skLineSegment(sketch, "E17.right", {"start": v(-300, -70.17) * mm, "end": v(-300, 71.26) * mm});
            skPoint(sketch, "E17.middle", {"position": v(-290, 0.54) * mm});
            skSolve(sketch);
        }
        {
            var Q0;
            {var subQ0=sQuery(id+"F15.wireOp",EDGE,"E17.bottom");Q0=makeQuery(id+"F15.imprint","IMPRINT",FACE,{"disambiguationData":[TD([[makeQuery(id+"F15.imprint","IMPRINT",EDGE,{"derivedFrom":subQ0}),-1.0]])]});}
            extrude(context, id + "F16", {"entities" : qUnion([Q0]), "oppositeDirection" : true, "depth" : 20 * mm, "offsetDistance" : 25 * mm});
        }
    });
